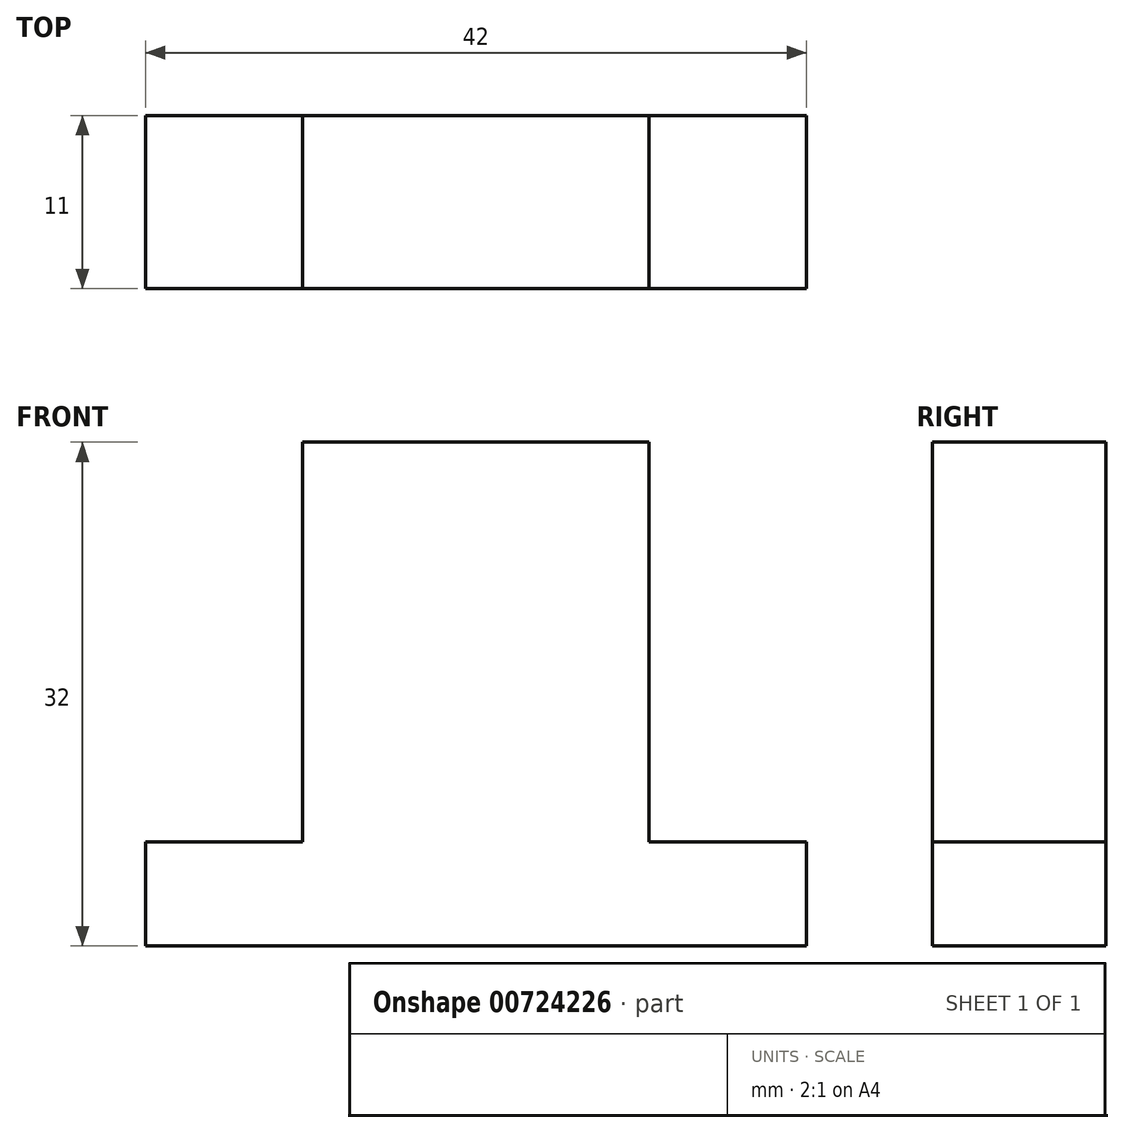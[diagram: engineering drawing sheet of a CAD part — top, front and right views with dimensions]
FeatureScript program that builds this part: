
annotation { "Feature Type Name" : "Feature", "Feature Type Description" : "" }
export const myFeature = defineFeature(function(context is Context, id is Id, definition is map)
    precondition{}
    {
        {
            var Q0;
            Q0=qCreatedBy(makeId("Front.planeOp"),FACE);
            var sketch = newSketch(context, id + "F0", { "sketchPlane" : qUnion([Q0])});
            skLineSegment(sketch, "E0.bottom", {"start": v(-27.92, 14.6) * mm, "end": v(14.08, 14.6) * mm});
            skLineSegment(sketch, "E0.top", {"start": v(-27.92, -17.4) * mm, "end": v(14.08, -17.4) * mm});
            skLineSegment(sketch, "E0.left", {"start": v(-27.92, 14.6) * mm, "end": v(-27.92, -17.4) * mm});
            skLineSegment(sketch, "E0.right", {"start": v(14.08, 14.6) * mm, "end": v(14.08, -17.4) * mm});
            skSolve(sketch);
        }
        {
            var Q0;
            Q0=makeQuery(id+"F0.imprint","IMPRINT",FACE,{"disambiguationData":[TD([[makeQuery(id+"F0.imprint","IMPRINT",EDGE,{"derivedFrom":sQuery(id+"F0.wireOp",EDGE,"E0.bottom")}),-1.0]])]});
            extrude(context, id + "F1", {"entities" : qUnion([Q0]), "depth" : 11 * mm, "offsetDistance" : 25.4 * mm});
        }
        {
            var Q0;
            Q0=makeQuery(id+"F1.opExtrude","SWEPT_FACE",FACE,{"disambiguationData":[OSD([sQuery(id+"F0.wireOp",EDGE,"E0.bottom")])]});
            var sketch = newSketch(context, id + "F2", { "sketchPlane" : qUnion([Q0])});
            skLineSegment(sketch, "E1", {"start": v(-17.92, -11) * mm, "end": v(-17.92, 0) * mm});
            skLineSegment(sketch, "E2", {"start": v(4.08, -11) * mm, "end": v(4.08, 0) * mm});
            skSolve(sketch);
        }
        {
            var Q0;
            Q0 = qSketchRegion(id + "F2", true);
            var Q1;
            {var subQ0=sQuery(id+"F2.wireOp",EDGE,"E1");Q1=makeQuery(id+"F2.imprint","IMPRINT",FACE,{"disambiguationData":[TD([[makeQuery(id+"F2.imprint","IMPRINT",EDGE,{"derivedFrom":subQ0}),1.0]])]});}
            extrude(context, id + "F3", {"entities" : qUnion([Q0, Q1]), "operationType" : NewBodyOperationType.REMOVE, "oppositeDirection" : true, "depth" : 25.4 * mm, "offsetDistance" : 25.4 * mm});
        }
        {
            var Q0;
            {var subQ0=sQuery(id+"F2.wireOp",EDGE,"E2");Q0=makeQuery(id+"F2.imprint","IMPRINT",FACE,{"disambiguationData":[TD([[makeQuery(id+"F2.imprint","IMPRINT",EDGE,{"derivedFrom":subQ0}),-1.0]])]});}
            extrude(context, id + "F4", {"entities" : qUnion([Q0]), "operationType" : NewBodyOperationType.REMOVE, "oppositeDirection" : true, "depth" : 25.4 * mm, "offsetDistance" : 25.4 * mm});
        }
        {
            var Q0;
            Q0=makeQuery(id+"F1.opExtrude","CAP_FACE",FACE,{"disambiguationData":[OSD([sQuery(id+"F0.wireOp",EDGE,"E0.bottom"),sQuery(id+"F0.wireOp",EDGE,"E0.top"),sQuery(id+"F0.wireOp",EDGE,"E0.left"),sQuery(id+"F0.wireOp",EDGE,"E0.right")])],"isStart":true});
            var sketch = newSketch(context, id + "F5", { "sketchPlane" : qUnion([Q0])});
            skCircle(sketch, "E3", {"center": v(6.43, 3.47) * mm, "radius": 4 * mm});
            skSolve(sketch);
        }
        {
            var Q0;
            Q0=makeQuery(id+"F5.imprint","IMPRINT",FACE,{"disambiguationData":[TD([[makeQuery(id+"F5.imprint","IMPRINT",EDGE,{"derivedFrom":sQuery(id+"F5.wireOp",EDGE,"E3")}),-1.0]])]});
            var sketch = newSketch(context, id + "F6", { "sketchPlane" : qUnion([Q0])});
            skCircle(sketch, "E4", {"center": v(14.55, 11.66) * mm, "radius": 1.64 * mm});
            skCircle(sketch, "E5", {"center": v(14.65, 7.38) * mm, "radius": 0.6 * mm});
            skCircle(sketch, "E6", {"center": v(15.28, 10.94) * mm, "radius": 1.43 * mm});
            skCircle(sketch, "E7", {"center": v(12.34, 9.2) * mm, "radius": 3.41 * mm});
            skCircle(sketch, "E8", {"center": v(13.94, 10.44) * mm, "radius": 0.94 * mm});
            skCircle(sketch, "E9", {"center": v(15.28, 10.94) * mm, "radius": 0.3 * mm});
            skSolve(sketch);
        }
        {
            var Q0;
            {var subQ0=sQuery(id+"F6.wireOp",EDGE,"E7");var subQ1=sQuery(id+"F6.wireOp",EDGE,"E4");var subQ2=makeQuery(id+"F6.imprint","INTERSECT",VERTEX,{"disambiguationData":[OD(0.0)],"derivedFrom":[subQ1,subQ0]});Q0=makeQuery(id+"F6.imprint","IMPRINT",FACE,{"disambiguationData":[TD([[makeQuery(id+"F6.imprint","IMPRINT",EDGE,{"disambiguationData":[TD([[subQ2,1.0]])],"derivedFrom":subQ1}),1.0]])]});}
            extrude(context, id + "F7", {"entities" : qUnion([Q0]), "operationType" : NewBodyOperationType.ADD, "oppositeDirection" : true, "depth" : 1.53 * mm, "offsetDistance" : 25.4 * mm});
        }
    });
